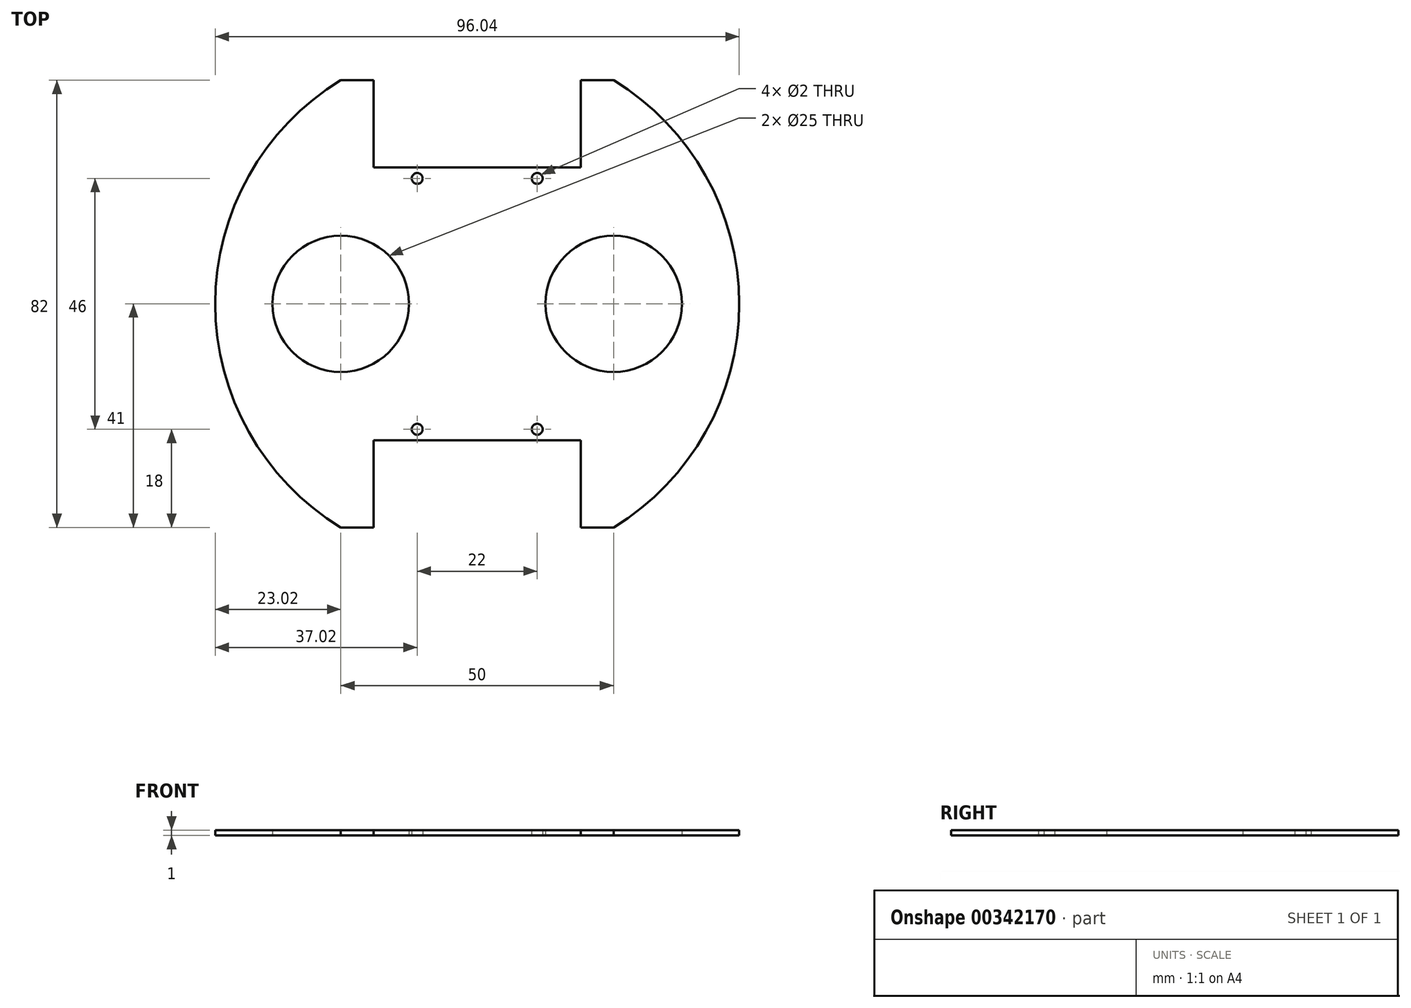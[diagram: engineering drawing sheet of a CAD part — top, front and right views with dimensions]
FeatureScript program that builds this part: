
annotation { "Feature Type Name" : "Feature", "Feature Type Description" : "" }
export const myFeature = defineFeature(function(context is Context, id is Id, definition is map)
    precondition{}
    {
        {
            var Q0;
            Q0=qCreatedBy(makeId("Top.planeOp"),FACE);
            var sketch = newSketch(context, id + "F0", { "sketchPlane" : qUnion([Q0])});
            skPoint(sketch, "E0", {"position": v(11, 23) * mm});
            skLineSegment(sketch, "E1", {"start": v(0, 25) * mm, "end": v(19, 25) * mm});
            skPoint(sketch, "E2.MirrorP", {"position": v(-11, 23) * mm});
            skPoint(sketch, "E3.MirrorP", {"position": v(11, -23) * mm});
            skPoint(sketch, "E4.MirrorP", {"position": v(-11, -23) * mm});
            skLineSegment(sketch, "E5.MirrorCS", {"start": v(0, -25) * mm, "end": v(19, -25) * mm});
            skLineSegment(sketch, "E6.MirrorCS", {"start": v(0, 25) * mm, "end": v(-19, 25) * mm});
            skLineSegment(sketch, "E7.MirrorCS", {"start": v(0, -25) * mm, "end": v(-19, -25) * mm});
            skLineSegment(sketch, "E8", {"start": v(19, 25) * mm, "end": v(19, 41) * mm});
            skLineSegment(sketch, "E9", {"start": v(19, 41) * mm, "end": v(25, 41) * mm});
            skLineSegment(sketch, "E10.MirrorCS", {"start": v(19, -41) * mm, "end": v(25, -41) * mm});
            skLineSegment(sketch, "E11.MirrorCS", {"start": v(19, -25) * mm, "end": v(19, -41) * mm});
            skPoint(sketch, "E12", {"position": v(25, 0) * mm});
            skArc(sketch, "E13", {"start": v(25, 41) * mm, "mid": v(48.02, 0) * mm, "end": v(25, -41) * mm});
            skCircle(sketch, "E14", {"center": v(25, 0) * mm, "radius": 12.5 * mm});
            skLineSegment(sketch, "E15.MirrorCS", {"start": v(-19, 25) * mm, "end": v(-19, 41) * mm});
            skLineSegment(sketch, "E16.MirrorCS", {"start": v(-19, -25) * mm, "end": v(-19, -41) * mm});
            skLineSegment(sketch, "E17.MirrorCS", {"start": v(-19, -41) * mm, "end": v(-25, -41) * mm});
            skCircle(sketch, "E18.MirrorC", {"center": v(-25, 0) * mm, "radius": 12.5 * mm});
            skLineSegment(sketch, "E19.MirrorCS", {"start": v(-19, 41) * mm, "end": v(-25, 41) * mm});
            skArc(sketch, "E20.MirrorCS", {"start": v(-25, 41) * mm, "mid": v(-48.02, 0) * mm, "end": v(-25, -41) * mm});
            skCircle(sketch, "E21", {"center": v(-11, 23) * mm, "radius": 1 * mm});
            skCircle(sketch, "E22.MirrorC", {"center": v(11, 23) * mm, "radius": 1 * mm});
            skCircle(sketch, "E23.MirrorC", {"center": v(-11, -23) * mm, "radius": 1 * mm});
            skCircle(sketch, "E24.MirrorC", {"center": v(11, -23) * mm, "radius": 1 * mm});
            skSolve(sketch);
        }
        {
            var Q0;
            Q0=makeQuery(id+"F0.imprint","IMPRINT",FACE,{"disambiguationData":[TD([[makeQuery(id+"F0.imprint","IMPRINT",EDGE,{"derivedFrom":sQuery(id+"F0.wireOp",EDGE,"E1")}),-1.0]])]});
            extrude(context, id + "F1", {"entities" : qUnion([Q0]), "depth" : 1 * mm});
        }
    });
